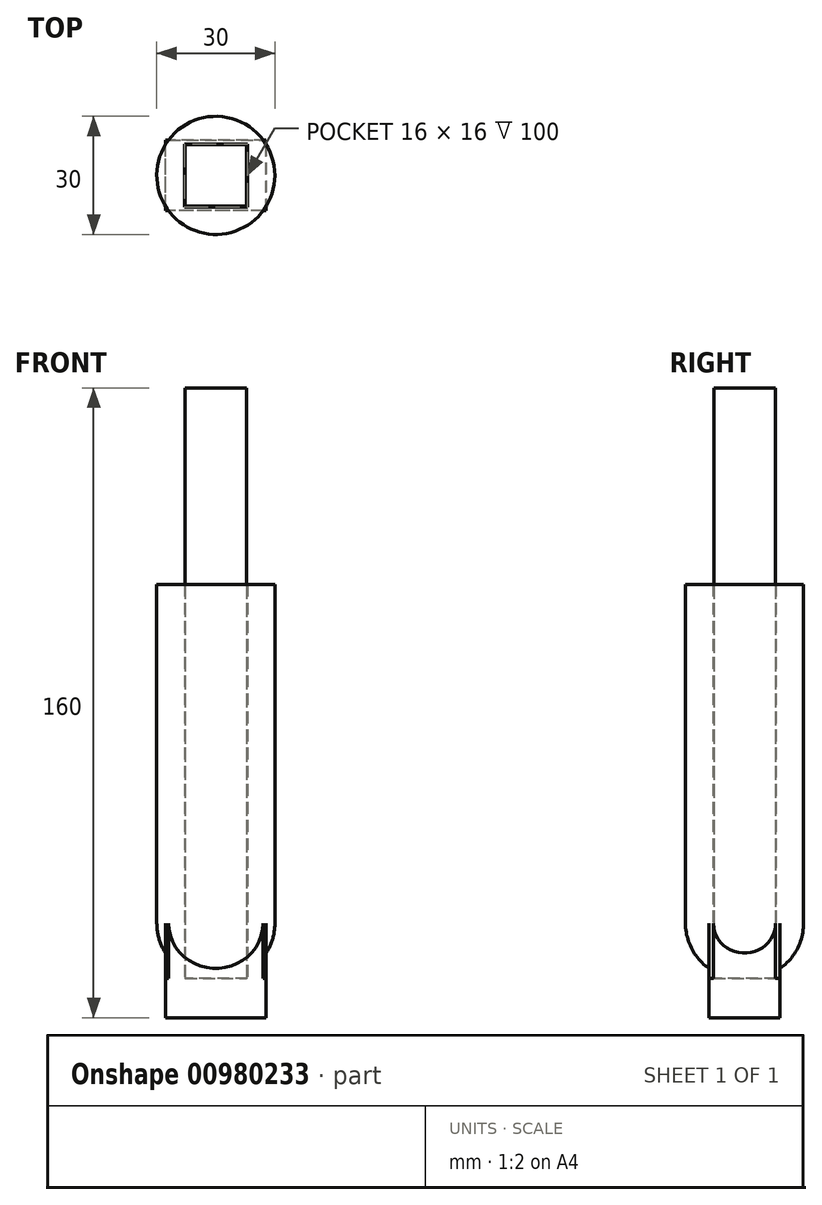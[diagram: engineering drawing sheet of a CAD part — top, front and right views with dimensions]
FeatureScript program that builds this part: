
annotation { "Feature Type Name" : "Feature", "Feature Type Description" : "" }
export const myFeature = defineFeature(function(context is Context, id is Id, definition is map)
    precondition{}
    {
        {
            var Q0;
            Q0=qCreatedBy(makeId("Top.planeOp"),FACE);
            var sketch = newSketch(context, id + "F0", { "sketchPlane" : qUnion([Q0])});
            skCircle(sketch, "E0", {"center": v(0, 0) * mm, "radius": 15 * mm});
            skLineSegment(sketch, "E1.bottom", {"start": v(8, 8) * mm, "end": v(-8, 8) * mm});
            skLineSegment(sketch, "E1.top", {"start": v(8, -8) * mm, "end": v(-8, -8) * mm});
            skLineSegment(sketch, "E1.left", {"start": v(8, 8) * mm, "end": v(8, -8) * mm});
            skLineSegment(sketch, "E1.right", {"start": v(-8, 8) * mm, "end": v(-8, -8) * mm});
            skLineSegment(sketch, "E2.bottom", {"start": v(10.6, -10.6) * mm, "end": v(-10.6, -10.6) * mm});
            skLineSegment(sketch, "E2.top", {"start": v(10.6, 10.6) * mm, "end": v(-10.6, 10.6) * mm});
            skLineSegment(sketch, "E2.left", {"start": v(10.6, -10.6) * mm, "end": v(10.6, 10.6) * mm});
            skLineSegment(sketch, "E2.right", {"start": v(-10.6, -10.6) * mm, "end": v(-10.6, 10.6) * mm});
            skSolve(sketch);
        }
        {
            assignVariable(context, id + "F1", {"name" : "cylinderHeight", "anyValue" : 100 * mm});
        }
        {
            var Q0;
            Q0=makeQuery(id+"F0.imprint","IMPRINT",FACE,{"disambiguationData":[TD([[makeQuery(id+"F0.imprint","IMPRINT",EDGE,{"derivedFrom":sQuery(id+"F0.wireOp",EDGE,"E0")}),1.0]])]});
            var Q1;
            Q1=makeQuery(id+"F0.imprint","IMPRINT",FACE,{"disambiguationData":[TD([[makeQuery(id+"F0.imprint","IMPRINT",EDGE,{"derivedFrom":sQuery(id+"F0.wireOp",EDGE,"E1.bottom")}),-1.0]])]});
            extrude(context, id + "F2", {"entities" : qUnion([Q0, Q1]), "depth" : getVariable(context, 'cylinderHeight'), "offsetDistance" : 25 * mm});
        }
        {
            var Q0;
            Q0=qCreatedBy(makeId("Top.planeOp"),FACE);
            var sketch = newSketch(context, id + "F3", { "sketchPlane" : qUnion([Q0])});
            skLineSegment(sketch, "E3.bottom", {"start": v(12.75, -9) * mm, "end": v(-12.75, -9) * mm});
            skLineSegment(sketch, "E3.top", {"start": v(12.75, 9) * mm, "end": v(-12.75, 9) * mm});
            skLineSegment(sketch, "E3.left", {"start": v(12.75, -9) * mm, "end": v(12.75, 9) * mm});
            skLineSegment(sketch, "E3.right", {"start": v(-12.75, -9) * mm, "end": v(-12.75, 9) * mm});
            skPoint(sketch, "E3.middle", {"position": v(0, 0) * mm});
            skSolve(sketch);
        }
        {
            var Q0;
            Q0=makeQuery(id+"F3.imprint","IMPRINT",FACE,{"disambiguationData":[TD([[makeQuery(id+"F3.imprint","IMPRINT",EDGE,{"derivedFrom":sQuery(id+"F3.wireOp",EDGE,"E3.bottom")}),-1.0]])]});
            extrude(context, id + "F4", {"entities" : qUnion([Q0]), "operationType" : NewBodyOperationType.ADD, "oppositeDirection" : true, "depth" : 10 * mm, "offsetDistance" : 25 * mm});
        }
        {
            var Q0;
            {var subQ0=sQuery(id+"F0.wireOp",EDGE,"E0");var subQ1=makeQuery(id+"F2.opExtrude","SWEPT_FACE",FACE,{"disambiguationData":[OSD([subQ0])]});var subQ2=makeQuery(id+"F2.opExtrude","CAP_FACE",FACE,{"disambiguationData":[OSD([subQ0,sQuery(id+"F0.wireOp",EDGE,"E1.bottom"),sQuery(id+"F0.wireOp",EDGE,"E1.top"),sQuery(id+"F0.wireOp",EDGE,"E1.left"),sQuery(id+"F0.wireOp",EDGE,"E1.right")])],"isStart":true});var subQ3=sQuery(id+"F3.wireOp",EDGE,"E3.top");Q0=makeQuery(id+"F4.boolean.opBoolean","SPLIT",EDGE,{"disambiguationData":[topologyDisambiguationEdgeConnected([subQ1,subQ2]),TD([makeQuery(id+"F4.opExtrude","SWEPT_FACE",FACE,{"disambiguationData":[OSD([subQ3])]})])],"derivedFrom":makeQuery(id+"F2.opExtrude","CAP_EDGE",EDGE,{"disambiguationData":[OSD([subQ0])],"isStart":true})});}
            var Q1;
            {var subQ0=sQuery(id+"F0.wireOp",EDGE,"E0");var subQ1=makeQuery(id+"F2.opExtrude","SWEPT_FACE",FACE,{"disambiguationData":[OSD([subQ0])]});var subQ2=makeQuery(id+"F2.opExtrude","CAP_FACE",FACE,{"disambiguationData":[OSD([subQ0,sQuery(id+"F0.wireOp",EDGE,"E1.bottom"),sQuery(id+"F0.wireOp",EDGE,"E1.top"),sQuery(id+"F0.wireOp",EDGE,"E1.left"),sQuery(id+"F0.wireOp",EDGE,"E1.right")])],"isStart":true});var subQ3=sQuery(id+"F3.wireOp",EDGE,"E3.left");Q1=makeQuery(id+"F4.boolean.opBoolean","SPLIT",EDGE,{"disambiguationData":[topologyDisambiguationEdgeConnected([subQ1,subQ2]),TD([makeQuery(id+"F4.opExtrude","SWEPT_FACE",FACE,{"disambiguationData":[OSD([subQ3])]})])],"derivedFrom":makeQuery(id+"F2.opExtrude","CAP_EDGE",EDGE,{"disambiguationData":[OSD([subQ0])],"isStart":true})});}
            var Q2;
            {var subQ0=sQuery(id+"F0.wireOp",EDGE,"E0");var subQ1=makeQuery(id+"F2.opExtrude","SWEPT_FACE",FACE,{"disambiguationData":[OSD([subQ0])]});var subQ2=makeQuery(id+"F2.opExtrude","CAP_FACE",FACE,{"disambiguationData":[OSD([subQ0,sQuery(id+"F0.wireOp",EDGE,"E1.bottom"),sQuery(id+"F0.wireOp",EDGE,"E1.top"),sQuery(id+"F0.wireOp",EDGE,"E1.left"),sQuery(id+"F0.wireOp",EDGE,"E1.right")])],"isStart":true});var subQ3=sQuery(id+"F3.wireOp",EDGE,"E3.right");Q2=makeQuery(id+"F4.boolean.opBoolean","SPLIT",EDGE,{"disambiguationData":[topologyDisambiguationEdgeConnected([subQ1,subQ2]),TD([makeQuery(id+"F4.opExtrude","SWEPT_FACE",FACE,{"disambiguationData":[OSD([subQ3])]})])],"derivedFrom":makeQuery(id+"F2.opExtrude","CAP_EDGE",EDGE,{"disambiguationData":[OSD([subQ0])],"isStart":true})});}
            var Q3;
            {var subQ0=sQuery(id+"F0.wireOp",EDGE,"E0");var subQ1=makeQuery(id+"F2.opExtrude","SWEPT_FACE",FACE,{"disambiguationData":[OSD([subQ0])]});var subQ2=makeQuery(id+"F2.opExtrude","CAP_FACE",FACE,{"disambiguationData":[OSD([subQ0,sQuery(id+"F0.wireOp",EDGE,"E1.bottom"),sQuery(id+"F0.wireOp",EDGE,"E1.top"),sQuery(id+"F0.wireOp",EDGE,"E1.left"),sQuery(id+"F0.wireOp",EDGE,"E1.right")])],"isStart":true});var subQ3=sQuery(id+"F3.wireOp",EDGE,"E3.bottom");Q3=makeQuery(id+"F4.boolean.opBoolean","SPLIT",EDGE,{"disambiguationData":[topologyDisambiguationEdgeConnected([subQ1,subQ2]),TD([makeQuery(id+"F4.opExtrude","SWEPT_FACE",FACE,{"disambiguationData":[OSD([subQ3])]})])],"derivedFrom":makeQuery(id+"F2.opExtrude","CAP_EDGE",EDGE,{"disambiguationData":[OSD([subQ0])],"isStart":true})});}
            fillet(context, id + "F5", {"entities" : qUnion([Q0, Q1, Q2, Q3]), "radius" : 14 * mm, "tangentPropagation" : true, "allowEdgeOverflow" : false});
        }
        {
            var Q0;
            Q0=qCreatedBy(makeId("Top.planeOp"),FACE);
            var sketch = newSketch(context, id + "F6", { "sketchPlane" : qUnion([Q0])});
            skLineSegment(sketch, "E4.bottom", {"start": v(-7.8, -7.8) * mm, "end": v(7.8, -7.8) * mm});
            skLineSegment(sketch, "E4.top", {"start": v(-7.8, 7.8) * mm, "end": v(7.8, 7.8) * mm});
            skLineSegment(sketch, "E4.left", {"start": v(-7.8, -7.8) * mm, "end": v(-7.8, 7.8) * mm});
            skLineSegment(sketch, "E4.right", {"start": v(7.8, -7.8) * mm, "end": v(7.8, 7.8) * mm});
            skPoint(sketch, "E4.middle", {"position": v(0, 0) * mm});
            skSolve(sketch);
        }
        {
            var Q0;
            Q0=makeQuery(id+"F6.imprint","IMPRINT",FACE,{"disambiguationData":[TD([[makeQuery(id+"F6.imprint","IMPRINT",EDGE,{"derivedFrom":sQuery(id+"F6.wireOp",EDGE,"E4.bottom")}),1.0]])]});
            extrude(context, id + "F7", {"entities" : qUnion([Q0]), "depth" : getVariable(context, 'cylinderHeight') * 1.5, "offsetDistance" : 25 * mm});
        }
    });
